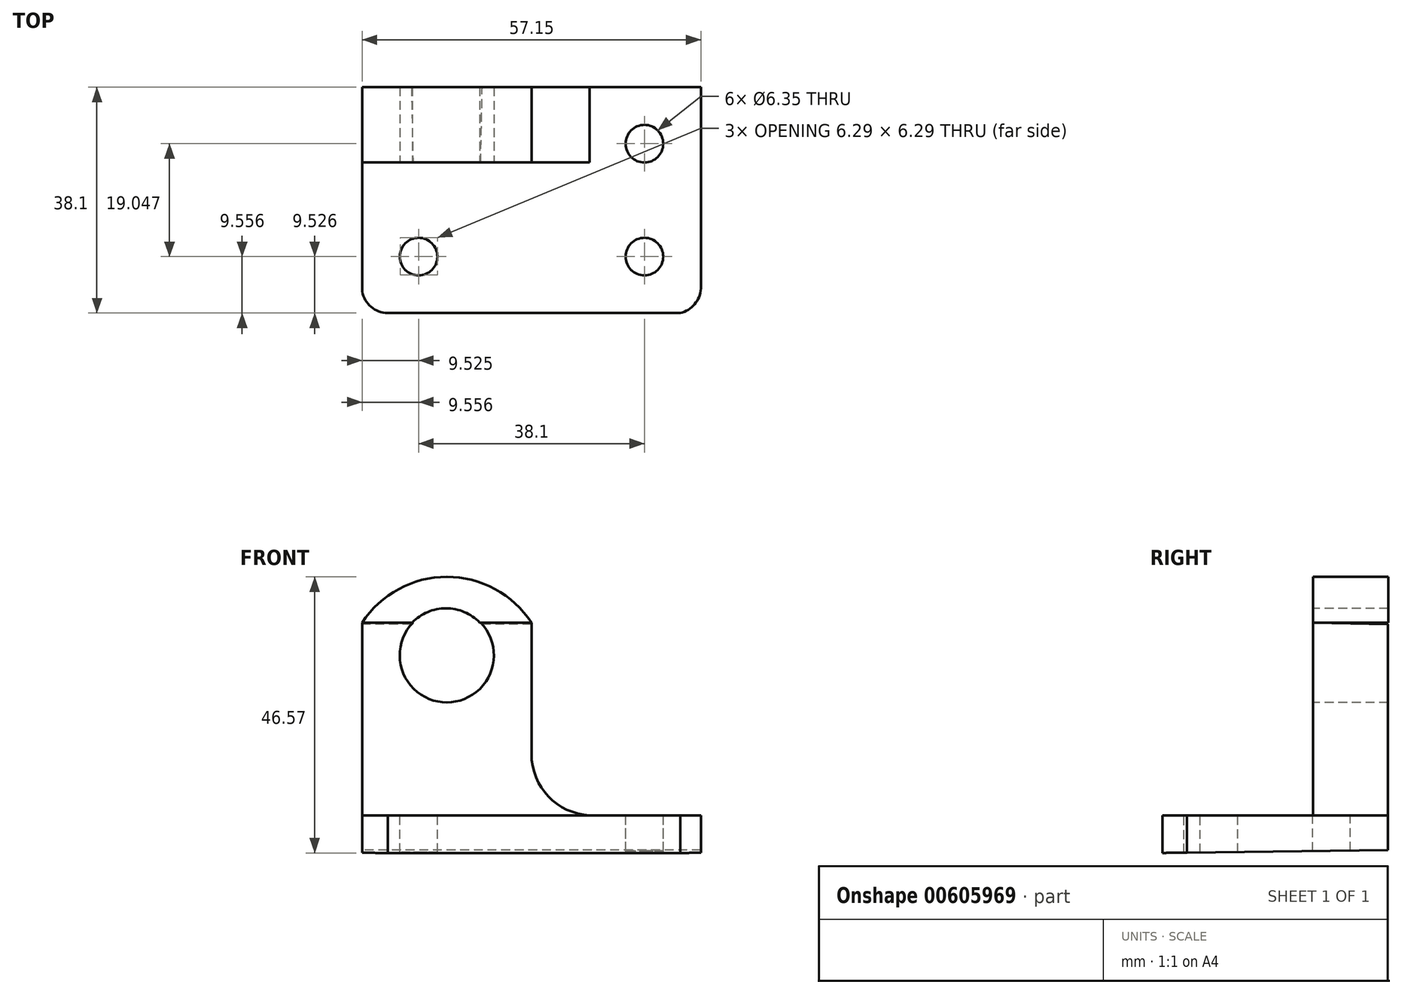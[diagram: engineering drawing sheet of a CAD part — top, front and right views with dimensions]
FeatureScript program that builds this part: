
annotation { "Feature Type Name" : "Feature", "Feature Type Description" : "" }
export const myFeature = defineFeature(function(context is Context, id is Id, definition is map)
    precondition{}
    {
        {
            var Q0;
            Q0=qCreatedBy(makeId("Right.planeOp"),FACE);
            var sketch = newSketch(context, id + "F0", { "sketchPlane" : qUnion([Q0])});
            skLineSegment(sketch, "E0", {"start": v(46.64, 46.19) * mm, "end": v(46.64, 8.09) * mm});
            skLineSegment(sketch, "E1", {"start": v(46.64, 8.09) * mm, "end": v(8.54, 7.6) * mm});
            skLineSegment(sketch, "E2", {"start": v(8.54, 7.6) * mm, "end": v(8.54, 13.96) * mm});
            skLineSegment(sketch, "E3", {"start": v(8.54, 13.96) * mm, "end": v(33.94, 13.96) * mm});
            skLineSegment(sketch, "E4", {"start": v(33.94, 13.96) * mm, "end": v(33.94, 46.46) * mm});
            skLineSegment(sketch, "E5", {"start": v(33.94, 46.46) * mm, "end": v(46.64, 46.19) * mm});
            skSolve(sketch);
        }
        {
            var Q0;
            Q0 = qSketchRegion(id + "F0", true);
            extrude(context, id + "F1", {"entities" : qUnion([Q0]), "depth" : 57.15 * mm, "offsetDistance" : 25.4 * mm});
        }
        {
            var Q0;
            Q0=makeQuery(id+"F1.opExtrude","SWEPT_FACE",FACE,{"disambiguationData":[OSD([sQuery(id+"F0.wireOp",EDGE,"E4")])]});
            var sketch = newSketch(context, id + "F2", { "sketchPlane" : qUnion([Q0])});
            skArc(sketch, "E6", {"start": v(28.58, 46.46) * mm, "mid": v(14.29, 54.18) * mm, "end": v(0, 46.46) * mm});
            skLineSegment(sketch, "E7", {"start": v(0, 46.46) * mm, "end": v(28.58, 46.46) * mm});
            skSolve(sketch);
        }
        {
            var Q0;
            Q0 = qSketchRegion(id + "F2", true);
            extrude(context, id + "F3", {"entities" : qUnion([Q0]), "oppositeDirection" : true, "depth" : 12.7 * mm, "offsetDistance" : 25.4 * mm});
        }
        {
            var Q0;
            Q0=makeQuery(id+"F1.opExtrude","SWEPT_FACE",FACE,{"disambiguationData":[OSD([sQuery(id+"F0.wireOp",EDGE,"E4")])]});
            var sketch = newSketch(context, id + "F4", { "sketchPlane" : qUnion([Q0])});
            skLineSegment(sketch, "E8", {"start": v(28.58, 46.46) * mm, "end": v(28.58, 24.26) * mm});
            skArc(sketch, "E9", {"start": v(28.58, 24.26) * mm, "mid": v(31.42, 17.15) * mm, "end": v(38.38, 13.96) * mm});
            skLineSegment(sketch, "E10", {"start": v(38.38, 13.96) * mm, "end": v(57.15, 13.96) * mm});
            skLineSegment(sketch, "E11", {"start": v(57.15, 13.96) * mm, "end": v(57.15, 46.46) * mm});
            skLineSegment(sketch, "E12", {"start": v(57.15, 46.46) * mm, "end": v(28.58, 46.46) * mm});
            skSolve(sketch);
        }
        {
            var Q0;
            Q0 = qSketchRegion(id + "F4", true);
            extrude(context, id + "F5", {"entities" : qUnion([Q0]), "operationType" : NewBodyOperationType.REMOVE, "oppositeDirection" : true, "depth" : 12.7 * mm, "offsetDistance" : 25.4 * mm});
        }
        {
            var Q0;
            Q0=makeQuery(id+"F1.opExtrude","SWEPT_FACE",FACE,{"disambiguationData":[OSD([sQuery(id+"F0.wireOp",EDGE,"E4")])]});
            var sketch = newSketch(context, id + "F6", { "sketchPlane" : qUnion([Q0])});
            skCircle(sketch, "E13", {"center": v(14.29, 40.95) * mm, "radius": 7.94 * mm});
            skSolve(sketch);
        }
        {
            var Q0;
            {var subQ0=sQuery(id+"F6.wireOp",EDGE,"E13");var subQ1=makeQuery(id+"F1.opExtrude","SWEPT_EDGE",EDGE,{"disambiguationData":[OSD([sQuery(id+"F0.wireOp",EDGE,"E4"),sQuery(id+"F0.wireOp",EDGE,"E5")])]});var subQ2=makeQuery(id+"F6.imprint","INTERSECT",VERTEX,{"disambiguationData":[OD(0.0)],"derivedFrom":[subQ1,subQ0]});Q0=makeQuery(id+"F6.imprint","IMPRINT",FACE,{"disambiguationData":[TD([[makeQuery(id+"F6.imprint","IMPRINT",EDGE,{"disambiguationData":[TD([[subQ2,-1.0]])],"derivedFrom":subQ0}),1.0]])]});}
            extrude(context, id + "F7", {"entities" : qUnion([Q0]), "operationType" : NewBodyOperationType.REMOVE, "oppositeDirection" : true, "depth" : 12.7 * mm, "offsetDistance" : 25.4 * mm});
        }
        {
            var Q0;
            Q0=makeQuery(id+"F3.opExtrude","CAP_FACE",FACE,{"disambiguationData":[OSD([sQuery(id+"F2.wireOp",EDGE,"E6"),sQuery(id+"F2.wireOp",EDGE,"E7")])],"isStart":true});
            var sketch = newSketch(context, id + "F8", { "sketchPlane" : qUnion([Q0])});
            skCircle(sketch, "E14", {"center": v(14.15, 40.93) * mm, "radius": 7.93 * mm});
            skSolve(sketch);
        }
        {
            var Q0;
            {var subQ0=sQuery(id+"F8.wireOp",EDGE,"E14");var subQ1=makeQuery(id+"F3.opExtrude","CAP_EDGE",EDGE,{"disambiguationData":[OSD([sQuery(id+"F2.wireOp",EDGE,"E7")])],"isStart":true});var subQ2=makeQuery(id+"F8.imprint","INTERSECT",VERTEX,{"disambiguationData":[OD(0.0)],"derivedFrom":[subQ1,subQ0]});Q0=makeQuery(id+"F8.imprint","IMPRINT",FACE,{"disambiguationData":[TD([[makeQuery(id+"F8.imprint","IMPRINT",EDGE,{"disambiguationData":[TD([[subQ2,1.0]])],"derivedFrom":subQ0}),1.0]])]});}
            extrude(context, id + "F9", {"entities" : qUnion([Q0]), "operationType" : NewBodyOperationType.REMOVE, "oppositeDirection" : true, "depth" : 12.7 * mm, "offsetDistance" : 25.4 * mm});
        }
        {
            var Q0;
            Q0=makeQuery(id+"F5.boolean.opBoolean","MERGE",FACE,{"derivedFrom":[makeQuery(id+"F1.opExtrude","SWEPT_FACE",FACE,{"disambiguationData":[OSD([sQuery(id+"F0.wireOp",EDGE,"E3")])]}),makeQuery(id+"F5.opExtrude","SWEPT_FACE",FACE,{"disambiguationData":[OSD([sQuery(id+"F4.wireOp",EDGE,"E10")])]})]});
            var sketch = newSketch(context, id + "F10", { "sketchPlane" : qUnion([Q0])});
            skArc(sketch, "E15", {"start": v(0, 13.93) * mm, "mid": v(0.97, 10.15) * mm, "end": v(4.53, 8.54) * mm});
            skLineSegment(sketch, "E16", {"start": v(0, 13.93) * mm, "end": v(0, 8.54) * mm});
            skLineSegment(sketch, "E17", {"start": v(0, 8.54) * mm, "end": v(4.53, 8.54) * mm});
            skSolve(sketch);
        }
        {
            var Q0;
            Q0 = qSketchRegion(id + "F10", true);
            extrude(context, id + "F11", {"entities" : qUnion([Q0]), "operationType" : NewBodyOperationType.REMOVE, "oppositeDirection" : true, "depth" : 6.35 * mm, "offsetDistance" : 25.4 * mm});
        }
        {
            var Q0;
            Q0=makeQuery(id+"F5.boolean.opBoolean","MERGE",FACE,{"derivedFrom":[makeQuery(id+"F1.opExtrude","SWEPT_FACE",FACE,{"disambiguationData":[OSD([sQuery(id+"F0.wireOp",EDGE,"E3")])]}),makeQuery(id+"F5.opExtrude","SWEPT_FACE",FACE,{"disambiguationData":[OSD([sQuery(id+"F4.wireOp",EDGE,"E10")])]})]});
            var sketch = newSketch(context, id + "F12", { "sketchPlane" : qUnion([Q0])});
            skArc(sketch, "E18", {"start": v(51.54, 8.54) * mm, "mid": v(55.53, 9.48) * mm, "end": v(57.15, 13.25) * mm});
            skLineSegment(sketch, "E19", {"start": v(51.54, 8.54) * mm, "end": v(57.15, 8.54) * mm});
            skLineSegment(sketch, "E20", {"start": v(57.15, 8.54) * mm, "end": v(57.15, 13.25) * mm});
            skSolve(sketch);
        }
        {
            var Q0;
            Q0 = qSketchRegion(id + "F12", true);
            extrude(context, id + "F13", {"entities" : qUnion([Q0]), "operationType" : NewBodyOperationType.REMOVE, "oppositeDirection" : true, "depth" : 6.35 * mm, "offsetDistance" : 25.4 * mm});
        }
        {
            var Q0;
            Q0=makeQuery(id+"F5.boolean.opBoolean","MERGE",FACE,{"derivedFrom":[makeQuery(id+"F1.opExtrude","SWEPT_FACE",FACE,{"disambiguationData":[OSD([sQuery(id+"F0.wireOp",EDGE,"E3")])]}),makeQuery(id+"F5.opExtrude","SWEPT_FACE",FACE,{"disambiguationData":[OSD([sQuery(id+"F4.wireOp",EDGE,"E10")])]})]});
            var sketch = newSketch(context, id + "F14", { "sketchPlane" : qUnion([Q0])});
            skCircle(sketch, "E21", {"center": v(9.53, 18.07) * mm, "radius": 3.18 * mm});
            skSolve(sketch);
        }
        {
            var Q0;
            Q0 = qSketchRegion(id + "F14", true);
            extrude(context, id + "F15", {"entities" : qUnion([Q0]), "operationType" : NewBodyOperationType.REMOVE, "oppositeDirection" : true, "depth" : 6.35 * mm, "offsetDistance" : 25.4 * mm});
        }
        {
            var Q0;
            Q0=makeQuery(id+"F5.boolean.opBoolean","MERGE",FACE,{"derivedFrom":[makeQuery(id+"F1.opExtrude","SWEPT_FACE",FACE,{"disambiguationData":[OSD([sQuery(id+"F0.wireOp",EDGE,"E3")])]}),makeQuery(id+"F5.opExtrude","SWEPT_FACE",FACE,{"disambiguationData":[OSD([sQuery(id+"F4.wireOp",EDGE,"E10")])]})]});
            var sketch = newSketch(context, id + "F16", { "sketchPlane" : qUnion([Q0])});
            skCircle(sketch, "E22", {"center": v(47.63, 18.07) * mm, "radius": 3.18 * mm});
            skSolve(sketch);
        }
        {
            var Q0;
            Q0 = qSketchRegion(id + "F16", true);
            extrude(context, id + "F17", {"entities" : qUnion([Q0]), "operationType" : NewBodyOperationType.REMOVE, "oppositeDirection" : true, "depth" : 6.35 * mm, "offsetDistance" : 25.4 * mm});
        }
        {
            var Q0;
            Q0=makeQuery(id+"F5.boolean.opBoolean","MERGE",FACE,{"derivedFrom":[makeQuery(id+"F1.opExtrude","SWEPT_FACE",FACE,{"disambiguationData":[OSD([sQuery(id+"F0.wireOp",EDGE,"E3")])]}),makeQuery(id+"F5.opExtrude","SWEPT_FACE",FACE,{"disambiguationData":[OSD([sQuery(id+"F4.wireOp",EDGE,"E10")])]})]});
            var sketch = newSketch(context, id + "F18", { "sketchPlane" : qUnion([Q0])});
            skCircle(sketch, "E23", {"center": v(47.63, 37.11) * mm, "radius": 3.18 * mm});
            skSolve(sketch);
        }
        {
            var Q0;
            Q0 = qSketchRegion(id + "F18", true);
            extrude(context, id + "F19", {"entities" : qUnion([Q0]), "operationType" : NewBodyOperationType.REMOVE, "oppositeDirection" : true, "depth" : 6.35 * mm, "offsetDistance" : 25.4 * mm});
        }
    });
